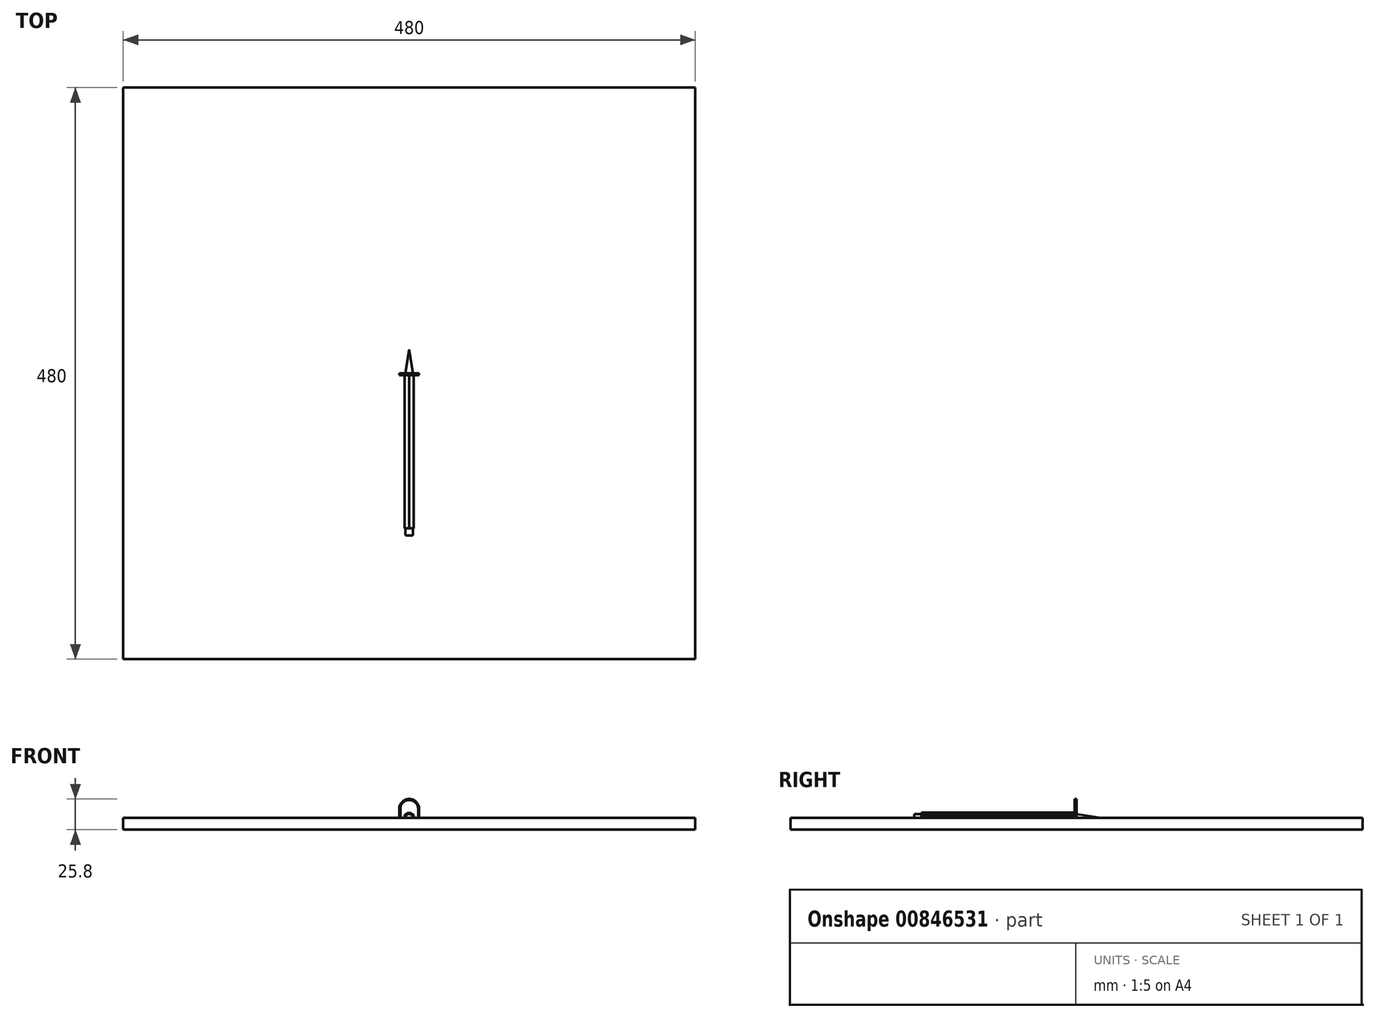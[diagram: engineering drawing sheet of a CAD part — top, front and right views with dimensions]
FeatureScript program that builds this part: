
annotation { "Feature Type Name" : "Feature", "Feature Type Description" : "" }
export const myFeature = defineFeature(function(context is Context, id is Id, definition is map)
    precondition{}
    {
        {
            var Q0;
            Q0=qCreatedBy(makeId("Front.planeOp"),FACE);
            var sketch = newSketch(context, id + "F0", { "sketchPlane" : qUnion([Q0])});
            skLineSegment(sketch, "E0", {"start": v(-7.5, 0) * mm, "end": v(7.5, 0) * mm});
            skLineSegment(sketch, "E1", {"start": v(7.5, 0) * mm, "end": v(7.5, 7.5) * mm});
            skLineSegment(sketch, "E2", {"start": v(-7.5, 0) * mm, "end": v(-7.5, 7.5) * mm});
            skArc(sketch, "E3", {"start": v(-7.5, 7.5) * mm, "mid": v(0, 15) * mm, "end": v(7.5, 7.5) * mm});
            skArc(sketch, "E4.0", {"start": v(-8.3, 7.5) * mm, "mid": v(0, 15.8) * mm, "end": v(8.3, 7.5) * mm});
            skLineSegment(sketch, "E4.1", {"start": v(-8.3, -0.8) * mm, "end": v(-8.3, 7.5) * mm});
            skLineSegment(sketch, "E4.2", {"start": v(-8.3, -0.8) * mm, "end": v(8.3, -0.8) * mm});
            skLineSegment(sketch, "E4.3", {"start": v(8.3, -0.8) * mm, "end": v(8.3, 7.5) * mm});
            skSolve(sketch);
        }
        {
            var Q0;
            Q0=qSketchRegion(id+"F0",true);
            extrude(context, id + "F1", {"entities" : qUnion([Q0]), "depth" : 1.5 * mm, "offsetDistance" : 25 * mm});
        }
        {
            var Q0;
            Q0=qCreatedBy(makeId("Top.planeOp"),FACE);
            var sketch = newSketch(context, id + "F2", { "sketchPlane" : qUnion([Q0])});
            skLineSegment(sketch, "E5.bottom", {"start": v(240, 240) * mm, "end": v(-240, 240) * mm});
            skLineSegment(sketch, "E5.top", {"start": v(240, -240) * mm, "end": v(-240, -240) * mm});
            skLineSegment(sketch, "E5.left", {"start": v(240, 240) * mm, "end": v(240, -240) * mm});
            skLineSegment(sketch, "E5.right", {"start": v(-240, 240) * mm, "end": v(-240, -240) * mm});
            skPoint(sketch, "E5.middle", {"position": v(0, 0) * mm});
            skSolve(sketch);
        }
        {
            var Q0;
            Q0=qSketchRegion(id+"F2",true);
            extrude(context, id + "F3", {"entities" : qUnion([Q0]), "oppositeDirection" : true, "depth" : 10 * mm, "offsetDistance" : 25 * mm});
        }
        {
            var Q0;
            Q0=qCreatedBy(makeId("Front.planeOp"),FACE);
            var sketch = newSketch(context, id + "F4", { "sketchPlane" : qUnion([Q0])});
            skCircle(sketch, "E6.cCircle", {"center": v(0, 0) * mm, "radius": 3.85 * mm, "construction": true});
            skLineSegment(sketch, "E6.0", {"start": v(3.85, 2.22) * mm, "end": v(3.85, -2.22) * mm});
            skLineSegment(sketch, "E6.1", {"start": v(3.85, -2.22) * mm, "end": v(0, -4.45) * mm});
            skLineSegment(sketch, "E6.2", {"start": v(0, -4.45) * mm, "end": v(-3.85, -2.22) * mm});
            skLineSegment(sketch, "E6.3", {"start": v(-3.85, -2.22) * mm, "end": v(-3.85, 2.22) * mm});
            skLineSegment(sketch, "E6.4", {"start": v(-3.85, 2.22) * mm, "end": v(0, 4.45) * mm});
            skLineSegment(sketch, "E6.5", {"start": v(0, 4.45) * mm, "end": v(3.85, 2.22) * mm});
            skPoint(sketch, "E6.0.midPoint", {"position": v(3.85, 0) * mm});
            skSolve(sketch);
        }
        {
            var Q0;
            Q0=qSketchRegion(id+"F4",true);
            extrude(context, id + "F5", {"entities" : qUnion([Q0]), "depth" : 130 * mm, "offsetDistance" : 25 * mm});
        }
        {
            var Q0;
            Q0=makeQuery(id+"F5.opExtrude","CAP_FACE",FACE,{"disambiguationData":[OSD([sQuery(id+"F4.wireOp",EDGE,"E6.0"),sQuery(id+"F4.wireOp",EDGE,"E6.1"),sQuery(id+"F4.wireOp",EDGE,"E6.2"),sQuery(id+"F4.wireOp",EDGE,"E6.3"),sQuery(id+"F4.wireOp",EDGE,"E6.4"),sQuery(id+"F4.wireOp",EDGE,"E6.5")])],"isStart":false});
            var sketch = newSketch(context, id + "F6", { "sketchPlane" : qUnion([Q0])});
            skCircle(sketch, "E7", {"center": v(0, 0) * mm, "radius": 3.13 * mm});
            skSolve(sketch);
        }
        {
            var Q0;
            Q0=qSketchRegion(id+"F6",true);
            extrude(context, id + "F7", {"entities" : qUnion([Q0]), "operationType" : NewBodyOperationType.ADD, "depth" : 6.25 * mm, "offsetDistance" : 25 * mm});
        }
        {
            var Q0;
            Q0=makeQuery(id+"F7.opExtrude","CAP_EDGE",EDGE,{"disambiguationData":[OSD([sQuery(id+"F6.wireOp",EDGE,"E7")])],"isStart":false});
            fillet(context, id + "F8", {"entities" : qUnion([Q0]), "radius" : 1 * mm, "tangentPropagation" : true, "allowEdgeOverflow" : false});
        }
        {
            var Q0;
            Q0=qCreatedBy(makeId("Top.planeOp"),FACE);
            var sketch = newSketch(context, id + "F9", { "sketchPlane" : qUnion([Q0])});
            skLineSegment(sketch, "E8", {"start": v(0, 0) * mm, "end": v(-3.12, 0) * mm});
            skLineSegment(sketch, "E9", {"start": v(-3.13, 0) * mm, "end": v(0, 20) * mm});
            skLineSegment(sketch, "E10", {"start": v(0, 20) * mm, "end": v(0, 0) * mm});
            skSolve(sketch);
        }
        {
            var Q0;
            Q0=qSketchRegion(id+"F9",true);
            var Q1;
            Q1=sQuery(id+"F9.wireOp",EDGE,"E10");
            revolve(context, id + "F10", {"operationType" : NewBodyOperationType.ADD, "surfaceOperationType" : NewSurfaceOperationType.NEW, "entities" : qUnion([Q0]), "axis" : qUnion([Q1]), "revolveType" : RevolveType.FULL});
        }
    });
